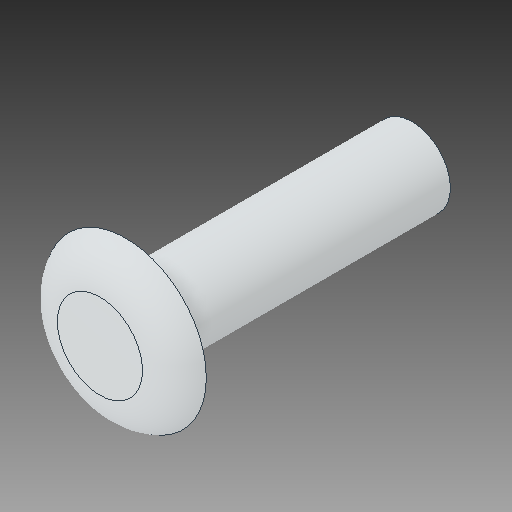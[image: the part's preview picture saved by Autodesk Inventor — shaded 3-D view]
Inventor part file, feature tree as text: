
AUTODESK INVENTOR PART (.ipt)
format: ipt  version: 2018 (Build 220112000, 112)  size: 109,568 bytes
history: native  units: in
note: dims shown in document units (in); Inventor stores cm internally (conversion verified against a paired STEP export)
features: fillet x1
ambient origin geometry x8: Origin, YZ Plane, XZ Plane, XY Plane, X Axis, Y Axis, Z Axis, Center Point
bodies: Solid1 (feature_tree)
feature tree (1):
  fillet  "Fillet1"  [1 undecoded]
note: 1 required parameter value undecoded (feature->parameter linkage not recoverable at this tier; creation-order binding heuristic only, values carry confidence <= 0.55)
